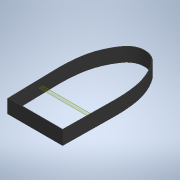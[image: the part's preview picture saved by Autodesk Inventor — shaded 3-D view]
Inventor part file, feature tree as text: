
AUTODESK INVENTOR PART (.ipt)
format: ipt  version: 2020 (Build 240168000, 168)  size: 166,400 bytes
history: native  units: mm
features: other x3, plane x1, sweep x1, sketch x1
ambient origin geometry x8: Origin, YZ Plane, XZ Plane, XY Plane, X Axis, Y Axis, Z Axis, Center Point
bodies: Solid1 (feature_tree)
feature tree (6):
  plane  "Work Plane1"
  sweep  "Sweep1"
  sketch  "Sketch3"  dims[d0=1.5mm d1=20.0mm d2=84.988716mm d3=0.0mm d4=0.0mm d7=10.0mm d8=80.7983mm d9=6.997044mm d10=8.0mm]
  parser-record x1  (decoder bookkeeping rows leaked as tree rows — omitted from the tree; the rows remain in map.json)
  other  "steering_queens_pair.iam"
  other  "hull_main:1"
note: 1 file-system path scrubbed to <path> (originals preserved in map.json)
